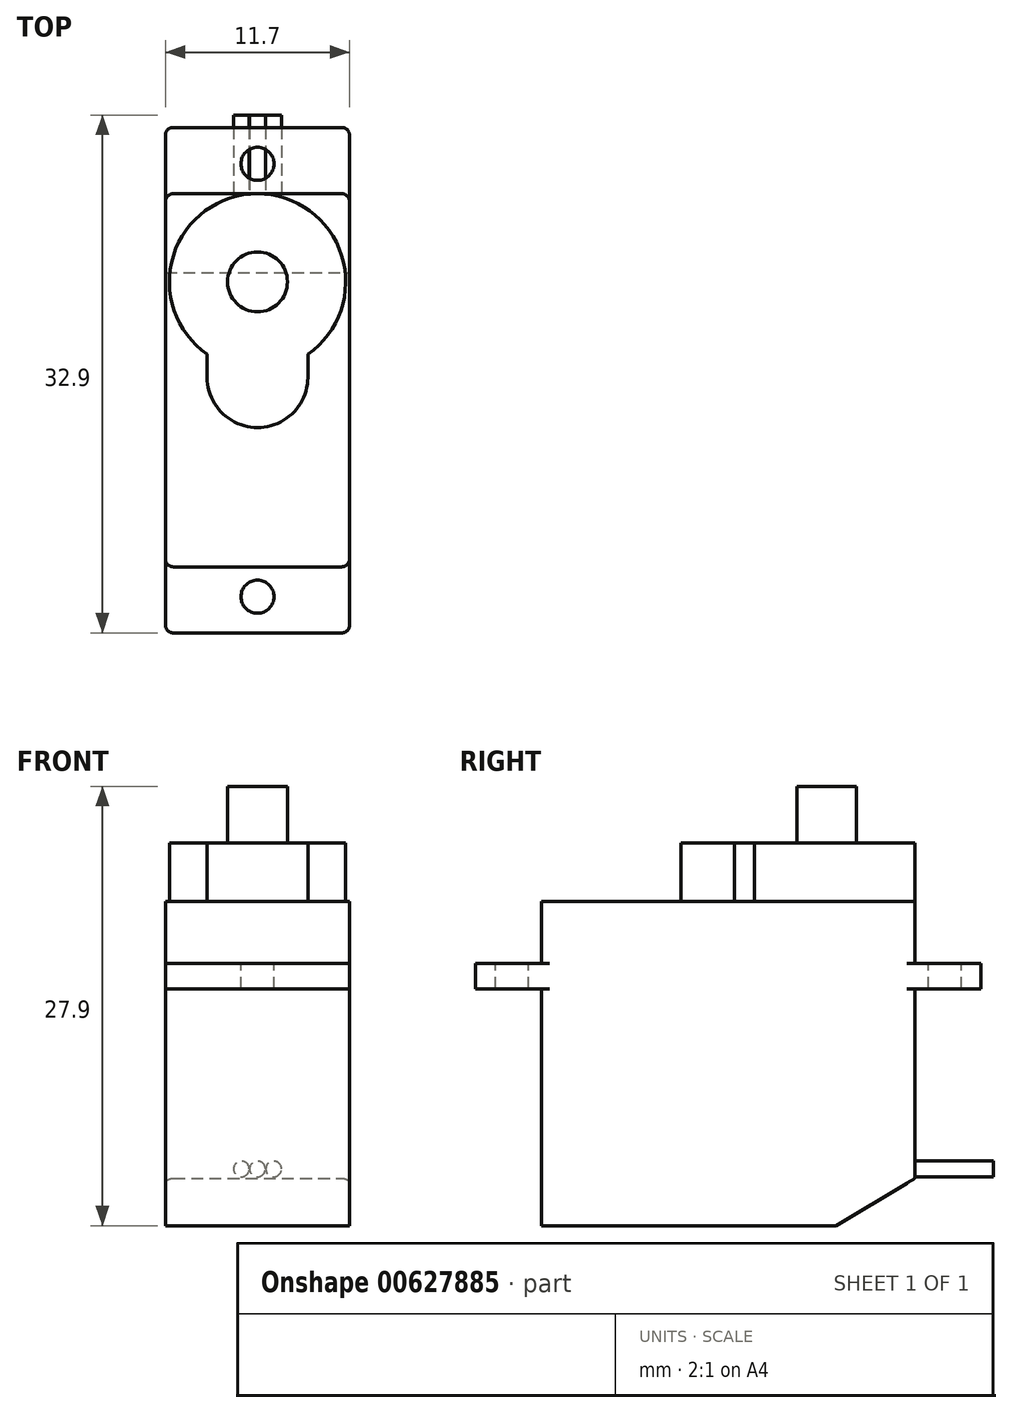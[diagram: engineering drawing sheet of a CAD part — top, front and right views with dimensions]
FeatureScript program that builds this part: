
annotation { "Feature Type Name" : "Feature", "Feature Type Description" : "" }
export const myFeature = defineFeature(function(context is Context, id is Id, definition is map)
    precondition{}
    {
        {
            var Q0;
            Q0=qCreatedBy(makeId("Right.planeOp"),FACE);
            var sketch = newSketch(context, id + "F0", { "sketchPlane" : qUnion([Q0])});
            skLineSegment(sketch, "E0", {"start": v(0, 0) * mm, "end": v(130.46, 0) * mm, "construction": true});
            skLineSegment(sketch, "E1.bottom", {"start": v(-11.85, 20.6) * mm, "end": v(11.85, 20.6) * mm});
            skLineSegment(sketch, "E1.top", {"start": v(-11.85, 0) * mm, "end": v(11.85, 0) * mm});
            skLineSegment(sketch, "E1.left", {"start": v(-11.85, 20.6) * mm, "end": v(-11.85, 0) * mm});
            skLineSegment(sketch, "E1.right", {"start": v(11.85, 20.6) * mm, "end": v(11.85, 0) * mm});
            skLineSegment(sketch, "E2", {"start": v(0, 0) * mm, "end": v(0, 95.99) * mm, "construction": true});
            skLineSegment(sketch, "E3.bottom", {"start": v(-11.85, 16.65) * mm, "end": v(-16.05, 16.65) * mm});
            skLineSegment(sketch, "E3.top", {"start": v(-11.85, 15.05) * mm, "end": v(-16.05, 15.05) * mm});
            skLineSegment(sketch, "E3.left", {"start": v(-11.85, 16.65) * mm, "end": v(-11.85, 15.05) * mm});
            skLineSegment(sketch, "E3.right", {"start": v(-16.05, 16.65) * mm, "end": v(-16.05, 15.05) * mm});
            skLineSegment(sketch, "E4.bottom", {"start": v(11.85, 16.65) * mm, "end": v(16.05, 16.65) * mm});
            skLineSegment(sketch, "E4.top", {"start": v(11.85, 15.05) * mm, "end": v(16.05, 15.05) * mm});
            skLineSegment(sketch, "E4.left", {"start": v(11.85, 16.65) * mm, "end": v(11.85, 15.05) * mm});
            skLineSegment(sketch, "E4.right", {"start": v(16.05, 16.65) * mm, "end": v(16.05, 15.05) * mm});
            skSolve(sketch);
        }
        {
            var Q0;
            {var subQ1=sQuery(id+"F0.wireOp",EDGE,"E1.bottom");var subQ2=sQuery(id+"F0.wireOp",EDGE,"E3.bottom");var subQ11=sQuery(id+"F0.wireOp",EDGE,"E4.bottom");Q0=qUnion([makeQuery(id+"F0.imprint","IMPRINT",FACE,{"disambiguationData":[TD([[makeQuery(id+"F0.imprint","IMPRINT",EDGE,{"derivedFrom":subQ2}),1.0]])]}),makeQuery(id+"F0.imprint","IMPRINT",FACE,{"disambiguationData":[TD([[makeQuery(id+"F0.imprint","IMPRINT",EDGE,{"derivedFrom":subQ11}),-1.0]])]}),makeQuery(id+"F0.imprint","IMPRINT",FACE,{"disambiguationData":[TD([[makeQuery(id+"F0.imprint","IMPRINT",EDGE,{"derivedFrom":subQ1}),-1.0]])]})]);}
            extrude(context, id + "F1", {"entities" : qUnion([Q0]), "depth" : (11.7 / 2) * mm, "offsetDistance" : 25 * mm, "hasSecondDirection" : true, "secondDirectionOppositeDirection" : true, "secondDirectionDepth" : (11.7 / 2) * mm});
        }
        {
            var Q0;
            Q0=makeQuery(id+"F1.opExtrude","SWEPT_FACE",FACE,{"disambiguationData":[OSD([sQuery(id+"F0.wireOp",EDGE,"E1.bottom")])]});
            var sketch = newSketch(context, id + "F2", { "sketchPlane" : qUnion([Q0])});
            skLineSegment(sketch, "E5", {"start": v(0, -11.85) * mm, "end": v(0, 11.85) * mm, "construction": true});
            skCircle(sketch, "E6", {"center": v(0, 6.25) * mm, "radius": 5.6 * mm});
            skCircle(sketch, "E7", {"center": v(0, 0.2) * mm, "radius": 3.2 * mm});
            skLineSegment(sketch, "E8", {"start": v(0, -3) * mm, "end": v(-8.21, -3) * mm, "construction": true});
            skLineSegment(sketch, "E9", {"start": v(-3.2, 0) * mm, "end": v(-3.2, 1.65) * mm});
            skLineSegment(sketch, "E10", {"start": v(3.2, 0) * mm, "end": v(3.2, 1.65) * mm});
            skSolve(sketch);
        }
        {
            var Q0;
            Q0 = qSketchRegion(id + "F2", true);
            var Q1;
            {var subQ0=sQuery(id+"F2.wireOp",EDGE,"E7");var subQ1=sQuery(id+"F2.wireOp",EDGE,"E6");var subQ2=makeQuery(id+"F2.imprint","INTERSECT",VERTEX,{"disambiguationData":[OD(0.0)],"derivedFrom":[subQ1,subQ0]});Q1=makeQuery(id+"F2.imprint","IMPRINT",FACE,{"disambiguationData":[TD([[makeQuery(id+"F2.imprint","IMPRINT",EDGE,{"disambiguationData":[TD([[subQ2,-1.0]])],"derivedFrom":subQ1}),1.0]])]});}
            extrude(context, id + "F3", {"entities" : qUnion([Q0, Q1]), "operationType" : NewBodyOperationType.ADD, "depth" : 3.7 * mm, "offsetDistance" : 25 * mm});
        }
        {
            var Q0;
            Q0=makeQuery(id+"F3.opExtrude","CAP_FACE",FACE,{"disambiguationData":[OSD([sQuery(id+"F2.wireOp",EDGE,"E6"),sQuery(id+"F2.wireOp",EDGE,"E7")])],"isStart":false});
            var sketch = newSketch(context, id + "F4", { "sketchPlane" : qUnion([Q0])});
            skLineSegment(sketch, "E11.0", {"start": v(-3.2, 1.65) * mm, "end": v(-3.2, 1.65) * mm});
            skCircle(sketch, "E12", {"center": v(0, 6.25) * mm, "radius": 1.9 * mm});
            skSolve(sketch);
        }
        {
            var Q0;
            Q0 = qSketchRegion(id + "F4", true);
            extrude(context, id + "F5", {"entities" : qUnion([Q0]), "operationType" : NewBodyOperationType.ADD, "depth" : 3.6 * mm, "offsetDistance" : 25 * mm});
        }
        {
            var Q0;
            Q0=makeQuery(id+"F1.opExtrude","SWEPT_FACE",FACE,{"disambiguationData":[OSD([sQuery(id+"F0.wireOp",EDGE,"E4.bottom")])]});
            var sketch = newSketch(context, id + "F6", { "sketchPlane" : qUnion([Q0])});
            skLineSegment(sketch, "E13", {"start": v(0, 16.05) * mm, "end": v(0, -16.05) * mm, "construction": true});
            skLineSegment(sketch, "E14.0", {"start": v(5.85, -16.05) * mm, "end": v(-5.85, -16.05) * mm, "construction": true});
            skCircle(sketch, "E15", {"center": v(0, 13.75) * mm, "radius": 1.05 * mm});
            skLineSegment(sketch, "E16", {"start": v(0, 0) * mm, "end": v(11.6, 0) * mm, "construction": true});
            skCircle(sketch, "E17.MirrorC", {"center": v(0, -13.75) * mm, "radius": 1.05 * mm});
            skSolve(sketch);
        }
        {
            var Q0;
            Q0 = qSketchRegion(id + "F6", true);
            extrude(context, id + "F7", {"entities" : qUnion([Q0]), "operationType" : NewBodyOperationType.REMOVE, "oppositeDirection" : true, "depth" : 10 * mm, "offsetDistance" : 25 * mm});
        }
        {
            var Q0;
            Q0=qCreatedBy(makeId("Right.planeOp"),FACE);
            var sketch = newSketch(context, id + "F8", { "sketchPlane" : qUnion([Q0])});
            skLineSegment(sketch, "E18.0", {"start": v(-11.85, 0) * mm, "end": v(11.85, 0) * mm});
            skLineSegment(sketch, "E19.0", {"start": v(11.85, 15.05) * mm, "end": v(11.85, 0) * mm});
            skLineSegment(sketch, "E20", {"start": v(6.85, 0) * mm, "end": v(11.85, 3) * mm});
            skSolve(sketch);
        }
        {
            var Q0;
            Q0 = qSketchRegion(id + "F8", true);
            extrude(context, id + "F9", {"entities" : qUnion([Q0]), "operationType" : NewBodyOperationType.REMOVE, "oppositeDirection" : true, "depth" : 25 * mm, "offsetDistance" : 25 * mm, "hasSecondDirection" : true, "secondDirectionOppositeDirection" : false, "secondDirectionDepth" : 25 * mm});
        }
        {
            var Q0;
            {var subQ0=sQuery(id+"F0.wireOp",EDGE,"E1.left");Q0=makeQuery(id+"F1.opExtrude","CAP_EDGE",EDGE,{"disambiguationData":[OSD([subQ0]),TDD([makeQuery(id+"F0.imprint","IMPRINT",EDGE,{"disambiguationData":[TD([[makeQuery(id+"F0.imprint","INTERSECT",VERTEX,{"derivedFrom":[sQuery(id+"F0.wireOp",EDGE,"E1.bottom"),subQ0]}),-1.0]])],"derivedFrom":subQ0})])],"isStart":false});}
            var Q1;
            {var subQ0=sQuery(id+"F0.wireOp",EDGE,"E1.left");Q1=makeQuery(id+"F1.opExtrude","CAP_EDGE",EDGE,{"disambiguationData":[OSD([subQ0]),TDD([makeQuery(id+"F0.imprint","IMPRINT",EDGE,{"disambiguationData":[TD([[makeQuery(id+"F0.imprint","INTERSECT",VERTEX,{"derivedFrom":[sQuery(id+"F0.wireOp",EDGE,"E1.bottom"),subQ0]}),-1.0]])],"derivedFrom":subQ0})])],"isStart":true});}
            var Q2;
            {var subQ0=sQuery(id+"F0.wireOp",EDGE,"E1.left");Q2=makeQuery(id+"F1.opExtrude","CAP_EDGE",EDGE,{"disambiguationData":[OSD([subQ0]),TDD([makeQuery(id+"F0.imprint","IMPRINT",EDGE,{"disambiguationData":[TD([[makeQuery(id+"F0.imprint","INTERSECT",VERTEX,{"derivedFrom":[sQuery(id+"F0.wireOp",EDGE,"E1.top"),subQ0]}),1.0]])],"derivedFrom":subQ0})])],"isStart":true});}
            var Q3;
            {var subQ0=sQuery(id+"F0.wireOp",EDGE,"E1.left");Q3=makeQuery(id+"F1.opExtrude","CAP_EDGE",EDGE,{"disambiguationData":[OSD([subQ0]),TDD([makeQuery(id+"F0.imprint","IMPRINT",EDGE,{"disambiguationData":[TD([[makeQuery(id+"F0.imprint","INTERSECT",VERTEX,{"derivedFrom":[sQuery(id+"F0.wireOp",EDGE,"E1.top"),subQ0]}),1.0]])],"derivedFrom":subQ0})])],"isStart":false});}
            var Q4;
            {var subQ0=sQuery(id+"F0.wireOp",EDGE,"E1.right");Q4=makeQuery(id+"F1.opExtrude","CAP_EDGE",EDGE,{"disambiguationData":[OSD([subQ0]),TDD([makeQuery(id+"F0.imprint","IMPRINT",EDGE,{"disambiguationData":[TD([[makeQuery(id+"F0.imprint","INTERSECT",VERTEX,{"derivedFrom":[sQuery(id+"F0.wireOp",EDGE,"E1.bottom"),subQ0]}),-1.0]])],"derivedFrom":subQ0})])],"isStart":false});}
            var Q5;
            {var subQ0=sQuery(id+"F0.wireOp",EDGE,"E1.right");Q5=makeQuery(id+"F1.opExtrude","CAP_EDGE",EDGE,{"disambiguationData":[OSD([subQ0]),TDD([makeQuery(id+"F0.imprint","IMPRINT",EDGE,{"disambiguationData":[TD([[makeQuery(id+"F0.imprint","INTERSECT",VERTEX,{"derivedFrom":[sQuery(id+"F0.wireOp",EDGE,"E1.bottom"),subQ0]}),-1.0]])],"derivedFrom":subQ0})])],"isStart":true});}
            var Q6;
            {var subQ0=sQuery(id+"F0.wireOp",EDGE,"E1.right");Q6=makeQuery(id+"F1.opExtrude","CAP_EDGE",EDGE,{"disambiguationData":[OSD([subQ0]),TDD([makeQuery(id+"F0.imprint","IMPRINT",EDGE,{"disambiguationData":[TD([[makeQuery(id+"F0.imprint","INTERSECT",VERTEX,{"derivedFrom":[sQuery(id+"F0.wireOp",EDGE,"E1.top"),subQ0]}),1.0]])],"derivedFrom":subQ0})])],"isStart":true});}
            var Q7;
            {var subQ0=sQuery(id+"F0.wireOp",EDGE,"E1.right");Q7=makeQuery(id+"F1.opExtrude","CAP_EDGE",EDGE,{"disambiguationData":[OSD([subQ0]),TDD([makeQuery(id+"F0.imprint","IMPRINT",EDGE,{"disambiguationData":[TD([[makeQuery(id+"F0.imprint","INTERSECT",VERTEX,{"derivedFrom":[sQuery(id+"F0.wireOp",EDGE,"E1.top"),subQ0]}),1.0]])],"derivedFrom":subQ0})])],"isStart":false});}
            var Q8;
            Q8=makeQuery(id+"F1.opExtrude","CAP_EDGE",EDGE,{"disambiguationData":[OSD([sQuery(id+"F0.wireOp",EDGE,"E4.right")])],"isStart":false});
            var Q9;
            Q9=makeQuery(id+"F1.opExtrude","CAP_EDGE",EDGE,{"disambiguationData":[OSD([sQuery(id+"F0.wireOp",EDGE,"E4.right")])],"isStart":true});
            var Q10;
            Q10=makeQuery(id+"F1.opExtrude","CAP_EDGE",EDGE,{"disambiguationData":[OSD([sQuery(id+"F0.wireOp",EDGE,"E3.right")])],"isStart":false});
            var Q11;
            Q11=makeQuery(id+"F1.opExtrude","CAP_EDGE",EDGE,{"disambiguationData":[OSD([sQuery(id+"F0.wireOp",EDGE,"E3.right")])],"isStart":true});
            fillet(context, id + "F10", {"entities" : qUnion([Q0, Q1, Q2, Q3, Q4, Q5, Q6, Q7, Q8, Q9, Q10, Q11]), "radius" : .5 * mm, "tangentPropagation" : true, "allowEdgeOverflow" : false});
        }
        {
            var Q0;
            {var subQ0=sQuery(id+"F0.wireOp",EDGE,"E1.right");Q0=makeQuery(id+"F1.opExtrude","SWEPT_FACE",FACE,{"disambiguationData":[OSD([subQ0]),TDD([makeQuery(id+"F0.imprint","IMPRINT",EDGE,{"disambiguationData":[TD([[makeQuery(id+"F0.imprint","INTERSECT",VERTEX,{"derivedFrom":[sQuery(id+"F0.wireOp",EDGE,"E1.top"),subQ0]}),1.0]])],"derivedFrom":subQ0})])]});}
            var sketch = newSketch(context, id + "F11", { "sketchPlane" : qUnion([Q0])});
            skLineSegment(sketch, "E21", {"start": v(0, 0) * mm, "end": v(0, 48.29) * mm, "construction": true});
            skCircle(sketch, "E22", {"center": v(0, 3.6) * mm, "radius": 0.5 * mm});
            skLineSegment(sketch, "E23", {"start": v(0, 3.6) * mm, "end": v(4.1, 3.6) * mm, "construction": true});
            skCircle(sketch, "E24", {"center": v(1.03, 3.6) * mm, "radius": 0.5 * mm});
            skCircle(sketch, "E25.MirrorC", {"center": v(-1.03, 3.6) * mm, "radius": 0.5 * mm});
            skSolve(sketch);
        }
        {
            var Q0;
            Q0 = qSketchRegion(id + "F11", true);
            extrude(context, id + "F12", {"entities" : qUnion([Q0]), "operationType" : NewBodyOperationType.ADD, "depth" : 5 * mm, "offsetDistance" : 25 * mm});
        }
    });
